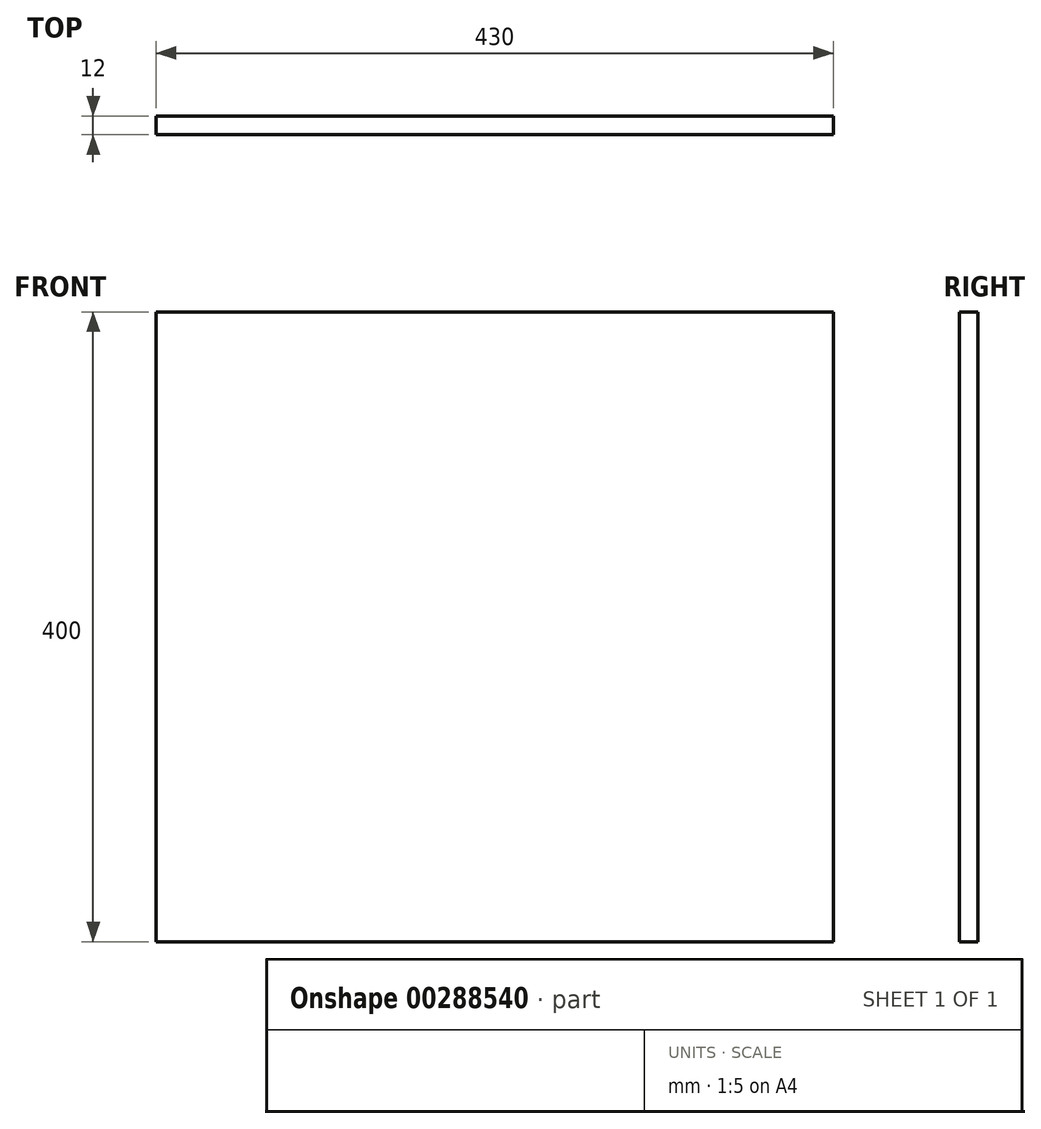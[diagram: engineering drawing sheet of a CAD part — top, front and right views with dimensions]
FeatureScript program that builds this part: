
annotation { "Feature Type Name" : "Feature", "Feature Type Description" : "" }
export const myFeature = defineFeature(function(context is Context, id is Id, definition is map)
    precondition{}
    {
        {
            var Q0;
            Q0=qCreatedBy(makeId("Front.planeOp"),FACE);
            var sketch = newSketch(context, id + "F0", { "sketchPlane" : qUnion([Q0])});
            skLineSegment(sketch, "E0.bottom", {"start": v(-215, 200) * mm, "end": v(215, 200) * mm});
            skLineSegment(sketch, "E0.top", {"start": v(-215, -200) * mm, "end": v(215, -200) * mm});
            skLineSegment(sketch, "E0.left", {"start": v(-215, 200) * mm, "end": v(-215, -200) * mm});
            skLineSegment(sketch, "E0.right", {"start": v(215, 200) * mm, "end": v(215, -200) * mm});
            skPoint(sketch, "E0.middle", {"position": v(0, 0) * mm});
            skSolve(sketch);
        }
        {
            var Q0;
            Q0 = qSketchRegion(id + "F0", true);
            extrude(context, id + "F1", {"entities" : qUnion([Q0]), "depth" : 12 * mm, "offsetDistance" : 25 * mm});
        }
    });
